# Revit family: Lustro_uchylne_dla_niepełnosprawnych_z_uchwytem 800 x 600 mm
name_source: partatom
category: Furniture
units: mm (PartAtom-declared; Revit-internal decimal feet)

## family parameters
Always vertical = Yes
Cut with Voids When Loaded = No
Host = Wall
Room Calculation Point = No
Shared = No

## types (1)
- N08024S
    Depth / Glebokosc = 800 mm  [stored 2.62467 ft]
    Description = Lustro uchylne dla niepełnosprawnych z uchwytem 800 x 600 mm montuje się naściennie w toaletach użytku publicznego. Świetnie nadaje się do łazienek restauracyjnych, szkolnych, szpitalnych i hotelowych. Znajduje swoje zastosowanie wszędzie tam, gdzie używają go osoby z problemami ruchowymi. Mogą one dostosować kąt nachylenia lustra do swoich potrzeb, co zwiększa ich wygodę i daje poczucie bezpieczeństwa i komfortu. Lustro uchylne dla niepełnosprawnych zrobiono z laminowanego szkła i włożono w stalową, mocną i trwałą ramę. Jest to solidny i funkcjonalny element wyposażenia toalet.
    Height / Wysokosc = 75 mm  [stored 0.246063 ft]
    Lustro = Lustro
    Manufacturer = FANECO.com
    Manufacturer code / Kod producenta = 5901764293422
    Material finish / Wykonczenie = Stal nierdzewna AISI 304 (rama, blacha), laminowane szkło (lustro)
    Material rama = Stal nierdzewna polerowana
    Product code / Kod produktu = N08024S
    Type Comments = Lustro uchylne dla niepełnosprawnych z uchwytem 800 x 600 mm stal szlachetna matowa
    URL = https://faneco.com
    Weight / Waga = 7.2 kg
    Width / Szerokosc = 600 mm  [stored 1.9685 ft]

note: [stored X ft] marks values corroborated as IEEE doubles in the binary element streams (Revit-internal decimal feet)

## geometry (parser evidence)
native form markers: Sweep x10
no freeform markers — native parametric forms only
